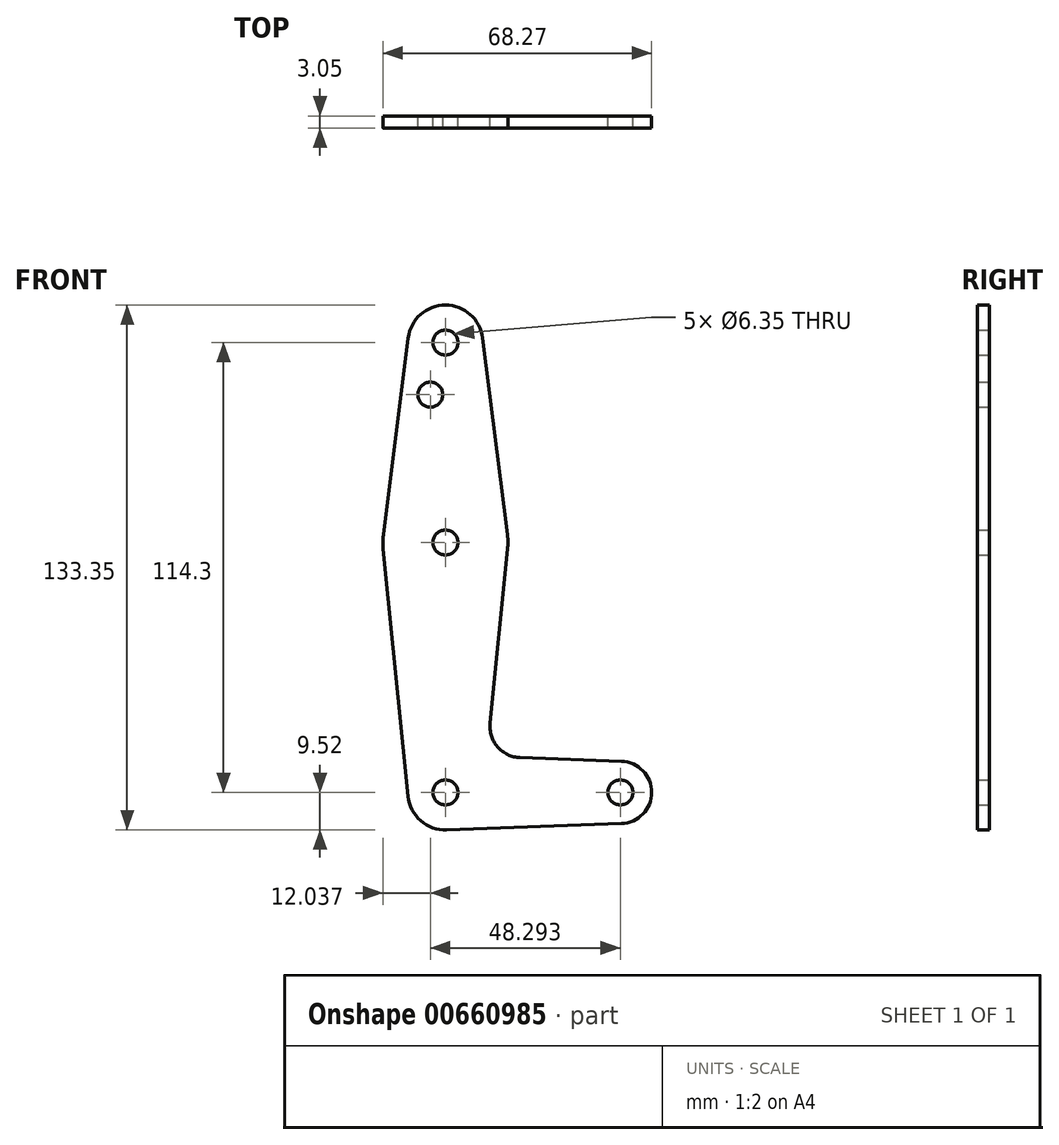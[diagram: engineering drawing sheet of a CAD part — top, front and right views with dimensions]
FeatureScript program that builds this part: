
annotation { "Feature Type Name" : "Feature", "Feature Type Description" : "" }
export const myFeature = defineFeature(function(context is Context, id is Id, definition is map)
    precondition{}
    {
        {
            var Q0;
            Q0=qCreatedBy(makeId("Front.planeOp"),FACE);
            var sketch = newSketch(context, id + "F0", { "sketchPlane" : qUnion([Q0])});
            skLineSegment(sketch, "E0", {"start": v(0, 114.3) * mm, "end": v(0, 0) * mm, "construction": true});
            skLineSegment(sketch, "E1", {"start": v(0, 0) * mm, "end": v(44.45, 0) * mm, "construction": true});
            skCircle(sketch, "E2", {"center": v(0, 114.3) * mm, "radius": 9.53 * mm});
            skCircle(sketch, "E3", {"center": v(0, 0) * mm, "radius": 9.53 * mm});
            skCircle(sketch, "E4", {"center": v(44.45, 0) * mm, "radius": 7.94 * mm});
            skCircle(sketch, "E5", {"center": v(0, 63.5) * mm, "radius": 15.88 * mm});
            skLineSegment(sketch, "E6", {"start": v(-9.45, 115.5) * mm, "end": v(-15.75, 65.48) * mm});
            skLineSegment(sketch, "E7", {"start": v(9.45, 115.5) * mm, "end": v(15.75, 65.48) * mm});
            skLineSegment(sketch, "E8", {"start": v(-15.8, 61.91) * mm, "end": v(-9.48, -0.95) * mm});
            skLineSegment(sketch, "E9", {"start": v(15.8, 61.91) * mm, "end": v(11.34, 17.6) * mm});
            skLineSegment(sketch, "E10", {"start": v(18.97, 8.85) * mm, "end": v(44.73, 7.93) * mm});
            skLineSegment(sketch, "E11", {"start": v(0.34, -9.52) * mm, "end": v(44.73, -7.93) * mm});
            skCircle(sketch, "E12", {"center": v(-3.84, 101.05) * mm, "radius": 3.18 * mm});
            skCircle(sketch, "E13", {"center": v(0, 63.5) * mm, "radius": 3.18 * mm});
            skCircle(sketch, "E14", {"center": v(0, 0) * mm, "radius": 3.18 * mm});
            skCircle(sketch, "E15", {"center": v(44.45, 0) * mm, "radius": 3.18 * mm});
            skCircle(sketch, "E16", {"center": v(0, 114.3) * mm, "radius": 3.18 * mm});
            skArc(sketch, "E17.filletArc", {"start": v(11.34, 17.6) * mm, "mid": v(13.26, 11.57) * mm, "end": v(18.97, 8.85) * mm});
            skSolve(sketch);
        }
        {
            var Q0;
            Q0 = qSketchRegion(id + "F0", true);
            extrude(context, id + "F1", {"entities" : qUnion([Q0]), "depth" : 3.05 * mm, "offsetDistance" : 25.4 * mm});
        }
    });
